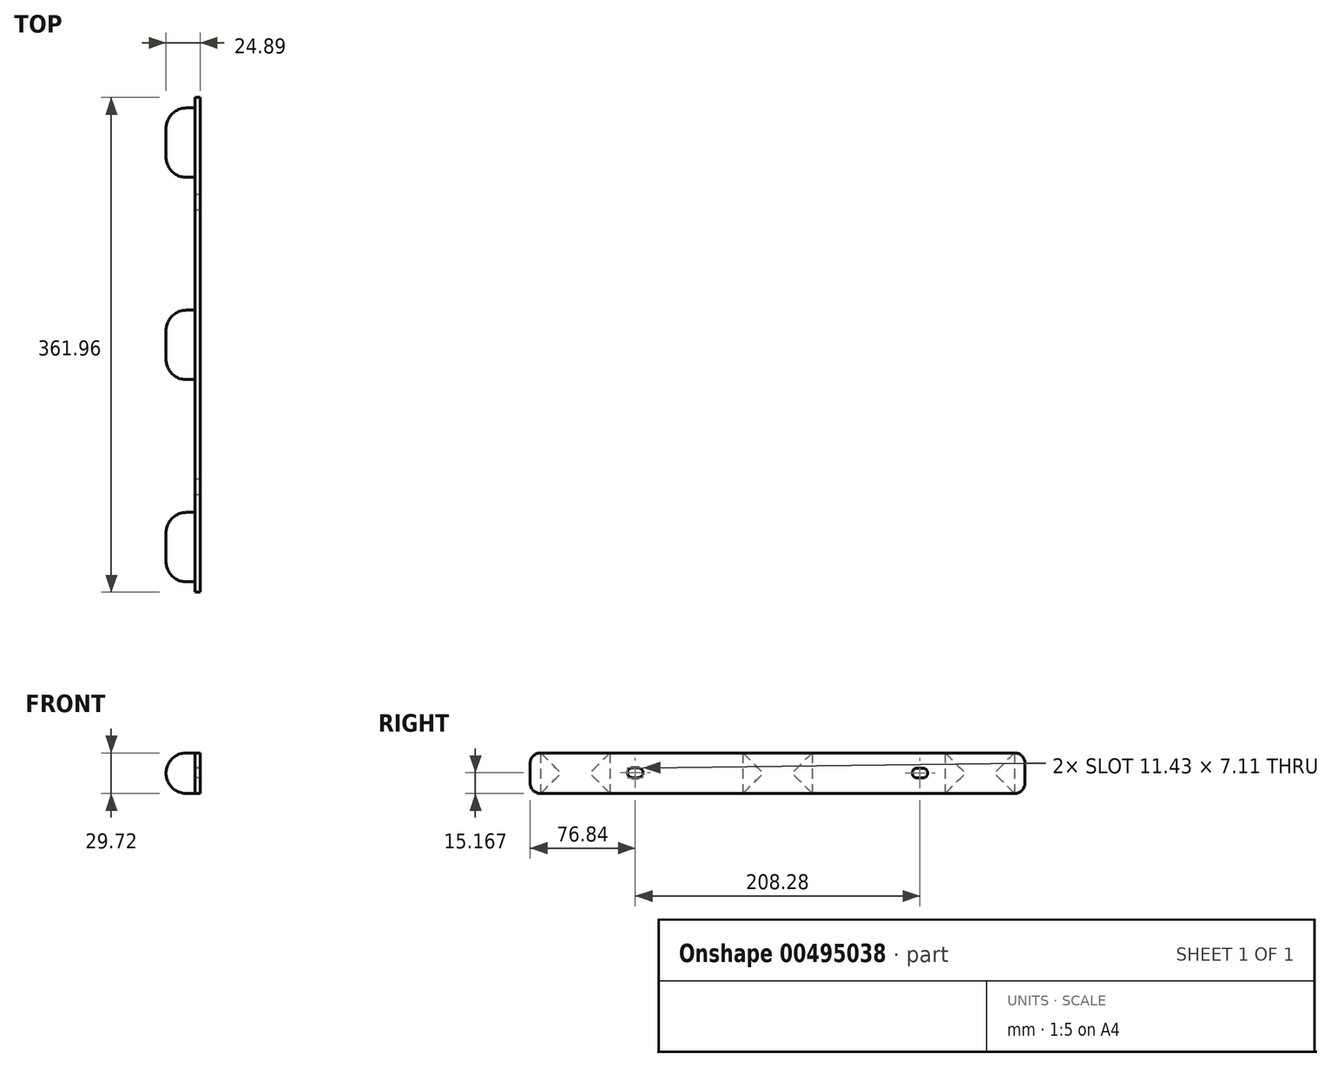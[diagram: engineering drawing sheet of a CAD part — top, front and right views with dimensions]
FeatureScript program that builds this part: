
annotation { "Feature Type Name" : "Feature", "Feature Type Description" : "" }
export const myFeature = defineFeature(function(context is Context, id is Id, definition is map)
    precondition{}
    {
        {
            var Q0;
            Q0=qCreatedBy(makeId("Right.planeOp"),FACE);
            var sketch = newSketch(context, id + "F0", { "sketchPlane" : qUnion([Q0])});
            skLineSegment(sketch, "E0.bottom", {"start": v(180.98, 14.86) * mm, "end": v(-180.98, 14.86) * mm});
            skLineSegment(sketch, "E0.top", {"start": v(180.98, -14.86) * mm, "end": v(-180.98, -14.86) * mm});
            skLineSegment(sketch, "E0.left", {"start": v(180.98, 14.86) * mm, "end": v(180.98, -14.86) * mm});
            skLineSegment(sketch, "E0.right", {"start": v(-180.98, 14.86) * mm, "end": v(-180.98, -14.86) * mm});
            skPoint(sketch, "E0.middle", {"position": v(0, 0) * mm});
            skSolve(sketch);
        }
        {
            var Q0;
            Q0=makeQuery(id+"F0.imprint","IMPRINT",FACE,{"disambiguationData":[TD([[makeQuery(id+"F0.imprint","IMPRINT",EDGE,{"derivedFrom":sQuery(id+"F0.wireOp",EDGE,"E0.bottom")}),1.0]])]});
            extrude(context, id + "F1", {"entities" : qUnion([Q0]), "depth" : 3.8 * mm});
        }
        {
            var Q0;
            Q0=makeQuery(id+"F1.opExtrude","SWEPT_EDGE",EDGE,{"disambiguationData":[OSD([sQuery(id+"F0.wireOp",EDGE,"E0.bottom"),sQuery(id+"F0.wireOp",EDGE,"E0.left")])]});
            var Q1;
            Q1=makeQuery(id+"F1.opExtrude","SWEPT_EDGE",EDGE,{"disambiguationData":[OSD([sQuery(id+"F0.wireOp",EDGE,"E0.top"),sQuery(id+"F0.wireOp",EDGE,"E0.left")])]});
            var Q2;
            Q2=makeQuery(id+"F1.opExtrude","SWEPT_EDGE",EDGE,{"disambiguationData":[OSD([sQuery(id+"F0.wireOp",EDGE,"E0.bottom"),sQuery(id+"F0.wireOp",EDGE,"E0.right")])]});
            var Q3;
            Q3=makeQuery(id+"F1.opExtrude","SWEPT_EDGE",EDGE,{"disambiguationData":[OSD([sQuery(id+"F0.wireOp",EDGE,"E0.top"),sQuery(id+"F0.wireOp",EDGE,"E0.right")])]});
            fillet(context, id + "F2", {"entities" : qUnion([Q0, Q1, Q2, Q3]), "radius" : 7.62 * mm, "tangentPropagation" : true, "allowEdgeOverflow" : false});
        }
        {
            var Q0;
            Q0=makeQuery(id+"F1.opExtrude","CAP_FACE",FACE,{"disambiguationData":[OSD([sQuery(id+"F0.wireOp",EDGE,"E0.bottom"),sQuery(id+"F0.wireOp",EDGE,"E0.top"),sQuery(id+"F0.wireOp",EDGE,"E0.left"),sQuery(id+"F0.wireOp",EDGE,"E0.right")])],"isStart":true});
            var sketch = newSketch(context, id + "F3", { "sketchPlane" : qUnion([Q0])});
            skLineSegment(sketch, "E1", {"start": v(-180.98, 0) * mm, "end": v(180.98, 0.39) * mm, "construction": true});
            skLineSegment(sketch, "E2.bottom", {"start": v(-106.3, 3.64) * mm, "end": v(-101.98, 3.64) * mm});
            skLineSegment(sketch, "E2.top", {"start": v(-106.3, -3.47) * mm, "end": v(-101.98, -3.47) * mm});
            skLineSegment(sketch, "E2.left", {"start": v(-109.86, 0.08) * mm, "end": v(-109.86, 0.08) * mm});
            skLineSegment(sketch, "E2.right", {"start": v(-98.43, 0.08) * mm, "end": v(-98.43, 0.08) * mm});
            skPoint(sketch, "E2.middle", {"position": v(-104.14, 0.08) * mm});
            skLineSegment(sketch, "E3.bottom", {"start": v(101.98, 3.86) * mm, "end": v(106.3, 3.86) * mm});
            skLineSegment(sketch, "E3.top", {"start": v(101.98, -3.25) * mm, "end": v(106.3, -3.25) * mm});
            skLineSegment(sketch, "E3.left", {"start": v(98.43, 0.3) * mm, "end": v(98.43, 0.3) * mm});
            skLineSegment(sketch, "E3.right", {"start": v(109.86, 0.3) * mm, "end": v(109.86, 0.3) * mm});
            skPoint(sketch, "E3.middle", {"position": v(104.14, 0.3) * mm});
            skLineSegment(sketch, "E4", {"start": v(0, 51.6) * mm, "end": v(0, -44.02) * mm, "construction": true});
            skPoint(sketch, "E4.endSnap0", {"position": v(0, -14.86) * mm});
            skPoint(sketch, "E5.visualSharp", {"position": v(-109.86, 3.64) * mm});
            skArc(sketch, "E5.filletArc", {"start": v(-106.3, 3.64) * mm, "mid": v(-108.81, 2.6) * mm, "end": v(-109.86, 0.08) * mm});
            skPoint(sketch, "E6.visualSharp", {"position": v(-98.43, 3.64) * mm});
            skArc(sketch, "E6.filletArc", {"start": v(-98.43, 0.08) * mm, "mid": v(-99.47, 2.6) * mm, "end": v(-101.98, 3.64) * mm});
            skPoint(sketch, "E7.visualSharp", {"position": v(-109.86, -3.47) * mm});
            skArc(sketch, "E7.filletArc", {"start": v(-109.86, 0.08) * mm, "mid": v(-108.81, -2.43) * mm, "end": v(-106.3, -3.47) * mm});
            skPoint(sketch, "E8.visualSharp", {"position": v(-98.43, -3.47) * mm});
            skArc(sketch, "E8.filletArc", {"start": v(-101.98, -3.47) * mm, "mid": v(-99.47, -2.43) * mm, "end": v(-98.43, 0.08) * mm});
            skPoint(sketch, "E9.visualSharp", {"position": v(98.43, 3.86) * mm});
            skArc(sketch, "E9.filletArc", {"start": v(101.98, 3.86) * mm, "mid": v(99.47, 2.82) * mm, "end": v(98.43, 0.3) * mm});
            skPoint(sketch, "E10.visualSharp", {"position": v(98.43, -3.25) * mm});
            skArc(sketch, "E10.filletArc", {"start": v(98.43, 0.3) * mm, "mid": v(99.47, -2.2) * mm, "end": v(101.98, -3.25) * mm});
            skPoint(sketch, "E11.visualSharp", {"position": v(109.86, -3.25) * mm});
            skArc(sketch, "E11.filletArc", {"start": v(106.3, -3.25) * mm, "mid": v(108.81, -2.2) * mm, "end": v(109.86, 0.3) * mm});
            skPoint(sketch, "E12.visualSharp", {"position": v(109.86, 3.86) * mm});
            skArc(sketch, "E12.filletArc", {"start": v(109.86, 0.3) * mm, "mid": v(108.81, 2.82) * mm, "end": v(106.3, 3.86) * mm});
            skSolve(sketch);
        }
        {
            var Q0;
            Q0=makeQuery(id+"F3.imprint","IMPRINT",FACE,{"disambiguationData":[TD([[makeQuery(id+"F3.imprint","IMPRINT",EDGE,{"derivedFrom":sQuery(id+"F3.wireOp",EDGE,"E2.bottom")}),-1.0]])]});
            var Q1;
            Q1=makeQuery(id+"F3.imprint","IMPRINT",FACE,{"disambiguationData":[TD([[makeQuery(id+"F3.imprint","IMPRINT",EDGE,{"derivedFrom":sQuery(id+"F3.wireOp",EDGE,"E3.bottom")}),-1.0]])]});
            extrude(context, id + "F4", {"entities" : qUnion([Q0, Q1]), "operationType" : NewBodyOperationType.REMOVE, "endBound" : BoundingType.UP_TO_NEXT, "oppositeDirection" : true, "depth" : 25.4 * mm});
        }
        {
            var Q0;
            Q0=makeQuery(id+"F1.opExtrude","CAP_FACE",FACE,{"disambiguationData":[OSD([sQuery(id+"F0.wireOp",EDGE,"E0.bottom"),sQuery(id+"F0.wireOp",EDGE,"E0.top"),sQuery(id+"F0.wireOp",EDGE,"E0.left"),sQuery(id+"F0.wireOp",EDGE,"E0.right")])],"isStart":true});
            var sketch = newSketch(context, id + "F5", { "sketchPlane" : qUnion([Q0])});
            skLineSegment(sketch, "E13.bottom", {"start": v(-173.36, 14.86) * mm, "end": v(-122.56, 14.86) * mm});
            skLineSegment(sketch, "E13.top", {"start": v(-173.36, -14.86) * mm, "end": v(-122.56, -14.86) * mm});
            skLineSegment(sketch, "E13.left", {"start": v(-173.36, 14.86) * mm, "end": v(-173.36, -14.86) * mm});
            skLineSegment(sketch, "E13.right", {"start": v(-122.56, 14.86) * mm, "end": v(-122.56, -14.86) * mm});
            skLineSegment(sketch, "E14.bottom", {"start": v(-25.4, 14.86) * mm, "end": v(25.4, 14.86) * mm});
            skLineSegment(sketch, "E14.top", {"start": v(-25.4, -14.86) * mm, "end": v(25.4, -14.86) * mm});
            skLineSegment(sketch, "E14.left", {"start": v(-25.4, 14.86) * mm, "end": v(-25.4, -14.86) * mm});
            skLineSegment(sketch, "E14.right", {"start": v(25.4, 14.86) * mm, "end": v(25.4, -14.86) * mm});
            skLineSegment(sketch, "E15.bottom", {"start": v(173.36, 14.86) * mm, "end": v(122.56, 14.86) * mm});
            skLineSegment(sketch, "E15.top", {"start": v(173.36, -14.86) * mm, "end": v(122.56, -14.86) * mm});
            skLineSegment(sketch, "E15.left", {"start": v(173.36, 14.86) * mm, "end": v(173.36, -14.86) * mm});
            skLineSegment(sketch, "E15.right", {"start": v(122.56, 14.86) * mm, "end": v(122.56, -14.86) * mm});
            skSolve(sketch);
        }
        {
            var Q0;
            Q0=makeQuery(id+"F5.imprint","IMPRINT",FACE,{"disambiguationData":[TD([[makeQuery(id+"F5.imprint","IMPRINT",EDGE,{"derivedFrom":sQuery(id+"F5.wireOp",EDGE,"E13.bottom")}),-1.0]])]});
            var Q1;
            Q1=makeQuery(id+"F5.imprint","IMPRINT",FACE,{"disambiguationData":[TD([[makeQuery(id+"F5.imprint","IMPRINT",EDGE,{"derivedFrom":sQuery(id+"F5.wireOp",EDGE,"E14.bottom")}),-1.0]])]});
            var Q2;
            Q2=makeQuery(id+"F5.imprint","IMPRINT",FACE,{"disambiguationData":[TD([[makeQuery(id+"F5.imprint","IMPRINT",EDGE,{"derivedFrom":sQuery(id+"F5.wireOp",EDGE,"E15.bottom")}),-1.0]])]});
            extrude(context, id + "F6", {"entities" : qUnion([Q0, Q1, Q2]), "depth" : 21.08 * mm});
        }
        {
            var Q0;
            Q0=makeQuery(id+"F6.opExtrude","CAP_EDGE",EDGE,{"disambiguationData":[OSD([sQuery(id+"F5.wireOp",EDGE,"E13.bottom")])],"isStart":false});
            var Q1;
            Q1=makeQuery(id+"F6.opExtrude","CAP_EDGE",EDGE,{"disambiguationData":[OSD([sQuery(id+"F5.wireOp",EDGE,"E13.left")])],"isStart":false});
            var Q2;
            Q2=makeQuery(id+"F6.opExtrude","CAP_EDGE",EDGE,{"disambiguationData":[OSD([sQuery(id+"F5.wireOp",EDGE,"E13.top")])],"isStart":false});
            var Q3;
            Q3=makeQuery(id+"F6.opExtrude","CAP_EDGE",EDGE,{"disambiguationData":[OSD([sQuery(id+"F5.wireOp",EDGE,"E13.right")])],"isStart":false});
            var Q4;
            Q4=makeQuery(id+"F6.opExtrude","CAP_EDGE",EDGE,{"disambiguationData":[OSD([sQuery(id+"F5.wireOp",EDGE,"E14.bottom")])],"isStart":false});
            var Q5;
            Q5=makeQuery(id+"F6.opExtrude","CAP_EDGE",EDGE,{"disambiguationData":[OSD([sQuery(id+"F5.wireOp",EDGE,"E14.left")])],"isStart":false});
            var Q6;
            Q6=makeQuery(id+"F6.opExtrude","CAP_EDGE",EDGE,{"disambiguationData":[OSD([sQuery(id+"F5.wireOp",EDGE,"E14.top")])],"isStart":false});
            var Q7;
            Q7=makeQuery(id+"F6.opExtrude","CAP_EDGE",EDGE,{"disambiguationData":[OSD([sQuery(id+"F5.wireOp",EDGE,"E14.right")])],"isStart":false});
            var Q8;
            Q8=makeQuery(id+"F6.opExtrude","CAP_EDGE",EDGE,{"disambiguationData":[OSD([sQuery(id+"F5.wireOp",EDGE,"E15.bottom")])],"isStart":false});
            var Q9;
            Q9=makeQuery(id+"F6.opExtrude","CAP_EDGE",EDGE,{"disambiguationData":[OSD([sQuery(id+"F5.wireOp",EDGE,"E15.right")])],"isStart":false});
            var Q10;
            Q10=makeQuery(id+"F6.opExtrude","CAP_EDGE",EDGE,{"disambiguationData":[OSD([sQuery(id+"F5.wireOp",EDGE,"E15.top")])],"isStart":false});
            var Q11;
            Q11=makeQuery(id+"F6.opExtrude","CAP_EDGE",EDGE,{"disambiguationData":[OSD([sQuery(id+"F5.wireOp",EDGE,"E15.left")])],"isStart":false});
            fillet(context, id + "F7", {"entities" : qUnion([Q0, Q1, Q2, Q3, Q4, Q5, Q6, Q7, Q8, Q9, Q10, Q11]), "radius" : 14.86 * mm, "tangentPropagation" : true, "allowEdgeOverflow" : false});
        }
    });
